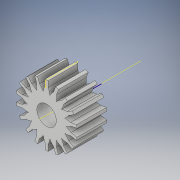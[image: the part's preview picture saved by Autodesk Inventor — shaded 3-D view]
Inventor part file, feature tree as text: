
AUTODESK INVENTOR PART (.ipt)
format: ipt  version: 2018 (Build 220112000, 112)  size: 207,872 bytes
history: native  units: in
note: dims shown in document units (in); Inventor stores cm internally (conversion verified against a paired STEP export)
features: sketch x3, extrude x2, plane x1, other x1, pattern_circular x1
ambient origin geometry x8: Origin, YZ Plane, XZ Plane, XY Plane, X Axis, Y Axis, Z Axis, Center Point
bodies: Solid1 (feature_tree)
feature tree (8):
  extrude  "Extrusion1"  Depth=0.128in
  extrude  "Extrusion2"  Depth=0.1969in
  plane  "Work Plane1"
  sketch  "Sketch3"  dims[d5=0.0197in d6=0.0197in d7=0.0236in d8=0.063in d10=0.1181in d11=0.1969in d12=0.0in d13=-0.0098in d14=7.0866in d15=360.0deg d18=0.0236in d19=0.1181in]
  other  "Work Axis1"
  pattern_circular  "Circular Pattern1"  [2 undecoded]
  sketch  "Sketch1"  dims[d0=0.2461in d1=0.128in]
  sketch  "Sketch2"  dims[d2=0.1969in d3=0.0in d4=0.0787in]
note: 2 required parameter values undecoded (feature->parameter linkage not recoverable at this tier; creation-order binding heuristic only, values carry confidence <= 0.55)
